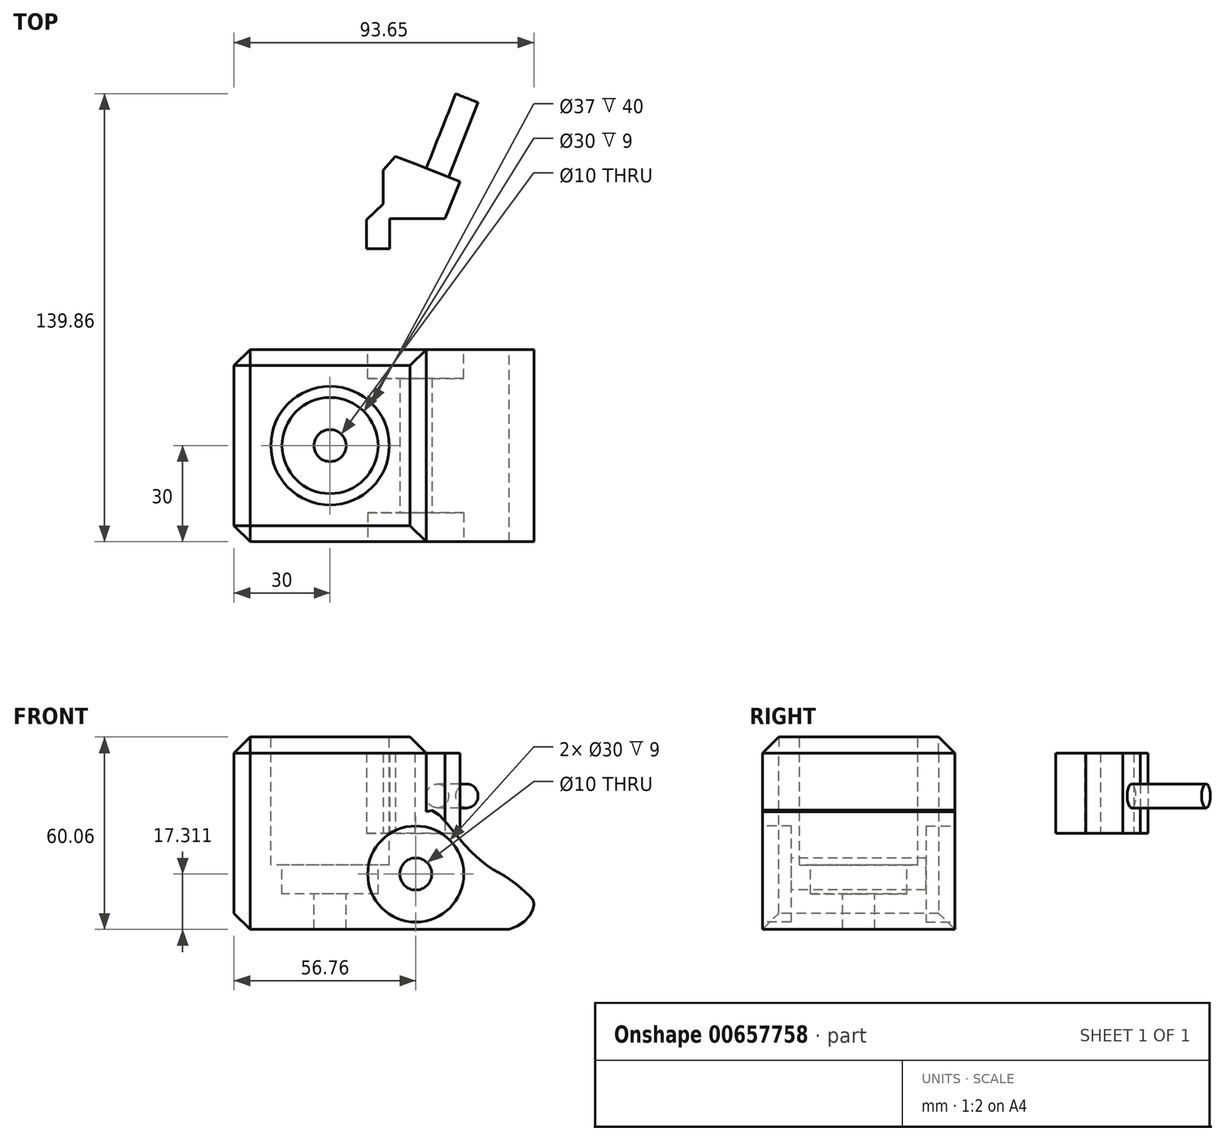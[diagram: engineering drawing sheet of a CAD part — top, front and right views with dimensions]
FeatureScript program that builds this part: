
annotation { "Feature Type Name" : "Feature", "Feature Type Description" : "" }
export const myFeature = defineFeature(function(context is Context, id is Id, definition is map)
    precondition{}
    {
        {
            var Q0;
            Q0=qCreatedBy(makeId("Front.planeOp"),FACE);
            var sketch = newSketch(context, id + "F0", { "sketchPlane" : qUnion([Q0])});
            skLineSegment(sketch, "E0.bottom", {"start": v(-30, 30) * mm, "end": v(30, 30) * mm});
            skLineSegment(sketch, "E0.top", {"start": v(-30, -30) * mm, "end": v(30, -30) * mm});
            skLineSegment(sketch, "E0.left", {"start": v(-30, 30) * mm, "end": v(-30, -30) * mm});
            skLineSegment(sketch, "E0.right", {"start": v(30, 30) * mm, "end": v(30, -30) * mm});
            skPoint(sketch, "E0.middle", {"position": v(0, 0) * mm});
            skFitSpline(sketch, "E1", {"points": [v(30, 6.69) * mm, v(40.63, -2.03) * mm, v(50.96, -11.35) * mm, v(56.43, -14.59) * mm, v(61.3, -18.64) * mm, v(63.52, -21.28) * mm, v(62.1, -26.14) * mm, v(53.2, -30.8) * mm, v(41.84, -30.6) * mm, v(32.93, -30.4) * mm, v(30, -30) * mm, v(30, 6.69) * mm]});
            skSolve(sketch);
        }
        {
            var Q0;
            {var subQ1=sQuery(id+"F0.wireOp",EDGE,"E0.bottom");Q0=makeQuery(id+"F0.imprint","IMPRINT",FACE,{"disambiguationData":[TD([[makeQuery(id+"F0.imprint","IMPRINT",EDGE,{"derivedFrom":subQ1}),-1.0]])]});}
            var Q1;
            {var subQ0=sQuery(id+"F0.wireOp",EDGE,"E1");Q1=makeQuery(id+"F0.imprint","IMPRINT",FACE,{"disambiguationData":[TD([[makeQuery(id+"F0.imprint","IMPRINT",EDGE,{"derivedFrom":subQ0}),-1.0]])]});}
            extrude(context, id + "F1", {"entities" : qUnion([Q0, Q1]), "depth" : 60 * mm, "offsetDistance" : 25 * mm});
        }
        {
            var Q0;
            Q0=makeQuery(id+"F1.opExtrude","SWEPT_FACE",FACE,{"disambiguationData":[OSD([sQuery(id+"F0.wireOp",EDGE,"E0.bottom")])]});
            var sketch = newSketch(context, id + "F2", { "sketchPlane" : qUnion([Q0])});
            skCircle(sketch, "E2", {"center": v(0, -30) * mm, "radius": 18.5 * mm});
            skPoint(sketch, "E2.centerSnap0", {"position": v(-30, -30) * mm});
            skSolve(sketch);
        }
        {
            var Q0;
            Q0 = qSketchRegion(id + "F2", true);
            var Q1;
            Q1=makeQuery(id+"F2.imprint","IMPRINT",FACE,{"disambiguationData":[TD([[makeQuery(id+"F2.imprint","IMPRINT",EDGE,{"derivedFrom":sQuery(id+"F2.wireOp",EDGE,"E2")}),1.0]])]});
            extrude(context, id + "F3", {"entities" : qUnion([Q0, Q1]), "operationType" : NewBodyOperationType.REMOVE, "oppositeDirection" : true, "depth" : 40 * mm, "offsetDistance" : 25 * mm});
        }
        {
            var Q0;
            Q0=makeQuery(id+"F3.boolean.opBoolean","COPY",FACE,{"derivedFrom":makeQuery(id+"F3.opExtrude","CAP_FACE",FACE,{"disambiguationData":[OSD([sQuery(id+"F2.wireOp",EDGE,"E2")])],"isStart":false})});
            var sketch = newSketch(context, id + "F4", { "sketchPlane" : qUnion([Q0])});
            skCircle(sketch, "E3", {"center": v(0, -30) * mm, "radius": 15 * mm});
            skSolve(sketch);
        }
        {
            var Q0;
            Q0=makeQuery(id+"F4.imprint","IMPRINT",FACE,{"disambiguationData":[TD([[makeQuery(id+"F4.imprint","IMPRINT",EDGE,{"derivedFrom":sQuery(id+"F4.wireOp",EDGE,"E3")}),1.0]])]});
            extrude(context, id + "F5", {"entities" : qUnion([Q0]), "operationType" : NewBodyOperationType.REMOVE, "oppositeDirection" : true, "depth" : 9 * mm, "offsetDistance" : 25 * mm});
        }
        {
            var Q0;
            Q0=makeQuery(id+"F5.boolean.opBoolean","COPY",FACE,{"derivedFrom":makeQuery(id+"F5.opExtrude","CAP_FACE",FACE,{"disambiguationData":[OSD([sQuery(id+"F4.wireOp",EDGE,"E3")])],"isStart":false})});
            var sketch = newSketch(context, id + "F6", { "sketchPlane" : qUnion([Q0])});
            skPoint(sketch, "E4", {"position": v(0, -30) * mm});
            skSolve(sketch);
        }
        {
            var Q0;
            Q0=sQuery(id+"F6.wireOp",VERTEX,"E4");
            var Q1;
            Q1=makeQuery(id+"F1.opExtrude","SWEPT_BODY",BODY,{"disambiguationData":[OSD([sQuery(id+"F0.wireOp",EDGE,"E0.bottom"),sQuery(id+"F0.wireOp",EDGE,"E0.top"),sQuery(id+"F0.wireOp",EDGE,"E0.left"),sQuery(id+"F0.wireOp",EDGE,"E0.right"),sQuery(id+"F0.wireOp",EDGE,"E1")])]});
            hole(context, id + "F7", {"style" : HoleStyle.SIMPLE, "endStyle" : HoleEndStyle.THROUGH, "holeDiameter" : 10 * mm, "majorDiameter" : 5 * mm, "isTappedThrough" : true, "tappedDepth" : 12 * mm, "tapClearance" : 3, "locations" : qUnion([Q0]), "scope" : qUnion([Q1])});
        }
        {
            var Q0;
            Q0=makeQuery(id+"F1.opExtrude","CAP_FACE",FACE,{"disambiguationData":[OSD([sQuery(id+"F0.wireOp",EDGE,"E0.bottom"),sQuery(id+"F0.wireOp",EDGE,"E0.top"),sQuery(id+"F0.wireOp",EDGE,"E0.left"),sQuery(id+"F0.wireOp",EDGE,"E0.right"),sQuery(id+"F0.wireOp",EDGE,"E1")])],"isStart":false});
            var sketch = newSketch(context, id + "F8", { "sketchPlane" : qUnion([Q0])});
            skCircle(sketch, "E5", {"center": v(26.76, -12.75) * mm, "radius": 15 * mm});
            skSolve(sketch);
        }
        {
            var Q0;
            Q0=makeQuery(id+"F8.imprint","IMPRINT",FACE,{"disambiguationData":[TD([[makeQuery(id+"F8.imprint","IMPRINT",EDGE,{"derivedFrom":sQuery(id+"F8.wireOp",EDGE,"E5")}),1.0]])]});
            extrude(context, id + "F9", {"entities" : qUnion([Q0]), "operationType" : NewBodyOperationType.REMOVE, "oppositeDirection" : true, "depth" : 9 * mm, "offsetDistance" : 25 * mm});
        }
        {
            var Q0;
            Q0=makeQuery(id+"F9.boolean.opBoolean","COPY",FACE,{"derivedFrom":makeQuery(id+"F9.opExtrude","CAP_FACE",FACE,{"disambiguationData":[OSD([sQuery(id+"F8.wireOp",EDGE,"E5")])],"isStart":false})});
            var sketch = newSketch(context, id + "F10", { "sketchPlane" : qUnion([Q0])});
            skPoint(sketch, "E6", {"position": v(26.76, -12.75) * mm});
            skSolve(sketch);
        }
        {
            var Q0;
            Q0=sQuery(id+"F10.wireOp",VERTEX,"E6");
            var Q1;
            Q1=makeQuery(id+"F1.opExtrude","SWEPT_BODY",BODY,{"disambiguationData":[OSD([sQuery(id+"F0.wireOp",EDGE,"E0.bottom"),sQuery(id+"F0.wireOp",EDGE,"E0.top"),sQuery(id+"F0.wireOp",EDGE,"E0.left"),sQuery(id+"F0.wireOp",EDGE,"E0.right"),sQuery(id+"F0.wireOp",EDGE,"E1")])]});
            hole(context, id + "F11", {"style" : HoleStyle.SIMPLE, "endStyle" : HoleEndStyle.THROUGH, "holeDiameter" : 10 * mm, "majorDiameter" : 5 * mm, "isTappedThrough" : true, "tappedDepth" : 12 * mm, "tapClearance" : 3, "locations" : qUnion([Q0]), "scope" : qUnion([Q1])});
        }
        {
            var Q0;
            Q0=makeQuery(id+"F1.opExtrude","CAP_FACE",FACE,{"disambiguationData":[OSD([sQuery(id+"F0.wireOp",EDGE,"E0.bottom"),sQuery(id+"F0.wireOp",EDGE,"E0.top"),sQuery(id+"F0.wireOp",EDGE,"E0.left"),sQuery(id+"F0.wireOp",EDGE,"E0.right"),sQuery(id+"F0.wireOp",EDGE,"E1")])],"isStart":true});
            var sketch = newSketch(context, id + "F12", { "sketchPlane" : qUnion([Q0])});
            skCircle(sketch, "E7", {"center": v(-26.76, -12.75) * mm, "radius": 15 * mm});
            skSolve(sketch);
        }
        {
            var Q0;
            Q0=makeQuery(id+"F12.imprint","IMPRINT",FACE,{"disambiguationData":[TD([[makeQuery(id+"F12.imprint","IMPRINT",EDGE,{"derivedFrom":sQuery(id+"F12.wireOp",EDGE,"E7")}),1.0]])]});
            extrude(context, id + "F13", {"entities" : qUnion([Q0]), "operationType" : NewBodyOperationType.REMOVE, "oppositeDirection" : true, "depth" : 9 * mm, "offsetDistance" : 25 * mm});
        }
        {
            var Q0;
            Q0=makeQuery(id+"F1.opExtrude","SWEPT_FACE",FACE,{"disambiguationData":[OSD([sQuery(id+"F0.wireOp",EDGE,"E0.left")])]});
            var Q1;
            Q1=makeQuery(id+"F1.opExtrude","CAP_EDGE",EDGE,{"disambiguationData":[OSD([sQuery(id+"F0.wireOp",EDGE,"E0.bottom")])],"isStart":true});
            var Q2;
            Q2=makeQuery(id+"F1.opExtrude","CAP_EDGE",EDGE,{"disambiguationData":[OSD([sQuery(id+"F0.wireOp",EDGE,"E0.bottom")])],"isStart":false});
            var Q3;
            Q3=makeQuery(id+"F1.opExtrude","SWEPT_EDGE",EDGE,{"disambiguationData":[OSD([sQuery(id+"F0.wireOp",EDGE,"E0.bottom"),sQuery(id+"F0.wireOp",EDGE,"E0.right")])]});
            chamfer(context, id + "F14", {"entities" : qUnion([Q0, Q1, Q2, Q3]), "width" : 5 * mm, "tangentPropagation" : true});
        }
        {
            var Q0;
            Q0=makeQuery(id+"F1.opExtrude","CAP_FACE",FACE,{"disambiguationData":[OSD([sQuery(id+"F0.wireOp",EDGE,"E0.bottom"),sQuery(id+"F0.wireOp",EDGE,"E0.top"),sQuery(id+"F0.wireOp",EDGE,"E0.left"),sQuery(id+"F0.wireOp",EDGE,"E0.right"),sQuery(id+"F0.wireOp",EDGE,"E1")])],"isStart":false});
            var sketch = newSketch(context, id + "F15", { "sketchPlane" : qUnion([Q0])});
            skSolve(sketch);
        }
        {
            var Q0;
            {var subQ1=sQuery(id+"F0.wireOp",EDGE,"E1");Q0=makeQuery(id+"F15.imprint","IMPRINT",FACE,{"disambiguationData":[TD([[makeQuery(id+"F15.imprint","IMPRINT",EDGE,{"derivedFrom":makeQuery(id+"F1.opExtrude","CAP_EDGE",EDGE,{"disambiguationData":[OSD([subQ1])],"isStart":false})}),-1.0]])]});}
            var sketch = newSketch(context, id + "F16", { "sketchPlane" : qUnion([Q0])});
            skLineSegment(sketch, "E8", {"start": v(23.13, -30.06) * mm, "end": v(56.2, -30.06) * mm});
            skLineSegment(sketch, "E9", {"start": v(23.13, -30.06) * mm, "end": v(49.71, -33.59) * mm});
            skLineSegment(sketch, "E10", {"start": v(49.71, -33.59) * mm, "end": v(56.2, -30.06) * mm});
            skSolve(sketch);
        }
        {
            var Q0;
            Q0 = qSketchRegion(id + "F16", true);
            extrude(context, id + "F17", {"entities" : qUnion([Q0]), "operationType" : NewBodyOperationType.REMOVE, "oppositeDirection" : true, "depth" : 80 * mm, "offsetDistance" : 25 * mm});
        }
        {
            var Q0;
            Q0=qCreatedBy(makeId("Top.planeOp"),FACE);
            var sketch = newSketch(context, id + "F18", { "sketchPlane" : qUnion([Q0])});
            skLineSegment(sketch, "E11", {"start": v(26.53, 58) * mm, "end": v(40.52, 52.47) * mm});
            skLineSegment(sketch, "E12", {"start": v(40.52, 52.47) * mm, "end": v(35.93, 40.9) * mm});
            skLineSegment(sketch, "E13", {"start": v(35.93, 40.9) * mm, "end": v(30.6, 40.9) * mm});
            skLineSegment(sketch, "E14", {"start": v(30.6, 40.9) * mm, "end": v(27.1, 40.9) * mm});
            skLineSegment(sketch, "E15", {"start": v(27.1, 40.9) * mm, "end": v(18.66, 40.9) * mm});
            skLineSegment(sketch, "E16", {"start": v(18.66, 40.9) * mm, "end": v(18.66, 31.48) * mm});
            skLineSegment(sketch, "E17", {"start": v(18.66, 31.48) * mm, "end": v(11.37, 31.48) * mm});
            skLineSegment(sketch, "E18", {"start": v(11.37, 31.48) * mm, "end": v(11.37, 40.52) * mm});
            skLineSegment(sketch, "E19", {"start": v(11.37, 40.52) * mm, "end": v(16.61, 45.47) * mm});
            skLineSegment(sketch, "E20", {"start": v(16.61, 45.47) * mm, "end": v(16.61, 55.97) * mm});
            skLineSegment(sketch, "E21", {"start": v(16.61, 55.97) * mm, "end": v(20.4, 60.34) * mm});
            skLineSegment(sketch, "E22", {"start": v(20.4, 60.34) * mm, "end": v(26.53, 58) * mm});
            skSolve(sketch);
        }
        {
            var Q0;
            Q0=makeQuery(id+"F18.imprint","IMPRINT",FACE,{"disambiguationData":[TD([[makeQuery(id+"F18.imprint","IMPRINT",EDGE,{"derivedFrom":sQuery(id+"F18.wireOp",EDGE,"E11")}),-1.0]])]});
            extrude(context, id + "F19", {"entities" : qUnion([Q0]), "depth" : 25 * mm, "offsetDistance" : 25 * mm});
        }
        {
            var Q0;
            Q0=makeQuery(id+"F19.opExtrude","SWEPT_FACE",FACE,{"disambiguationData":[OSD([sQuery(id+"F18.wireOp",EDGE,"E11")])]});
            var sketch = newSketch(context, id + "F20", { "sketchPlane" : qUnion([Q0])});
            skCircle(sketch, "E23", {"center": v(-10.84, 11.63) * mm, "radius": 3.73 * mm});
            skPoint(sketch, "E23.centerSnap0", {"position": v(-10.84, 0) * mm});
            skSolve(sketch);
        }
        {
            var Q0;
            Q0=makeQuery(id+"F20.imprint","IMPRINT",FACE,{"disambiguationData":[TD([[makeQuery(id+"F20.imprint","IMPRINT",EDGE,{"derivedFrom":sQuery(id+"F20.wireOp",EDGE,"E23")}),1.0]])]});
            extrude(context, id + "F21", {"entities" : qUnion([Q0]), "operationType" : NewBodyOperationType.ADD, "depth" : 25 * mm, "offsetDistance" : 25 * mm});
        }
    });
